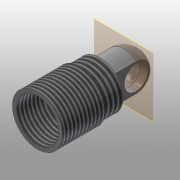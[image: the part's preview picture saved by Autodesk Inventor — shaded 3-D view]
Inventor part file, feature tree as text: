
AUTODESK INVENTOR PART (.ipt)
format: ipt  version: 2015 (Build 190159000, 159)  size: 145,920 bytes
history: native  units: mm
features: sketch x6, other x4, plane x1
ambient origin geometry x8: Origin, YZ Plane, XZ Plane, XY Plane, X Axis, Y Axis, Z Axis, Center Point
bodies: Solid1 (feature_tree)
feature tree (11):
  other  "500-106.ipt"
  other  "Solid1::500-106.ipt"
  other  "TaggingFeature1"
  sketch  "Sketch1"  dims[d0=10.0mm]
  sketch  "Sketch2"
  sketch  "Sketch3"
  sketch  "Sketch4"
  sketch  "Sketch5"
  sketch  "Sketch6"
  plane  "Work Plane1"
  other  "Work Axis1"
